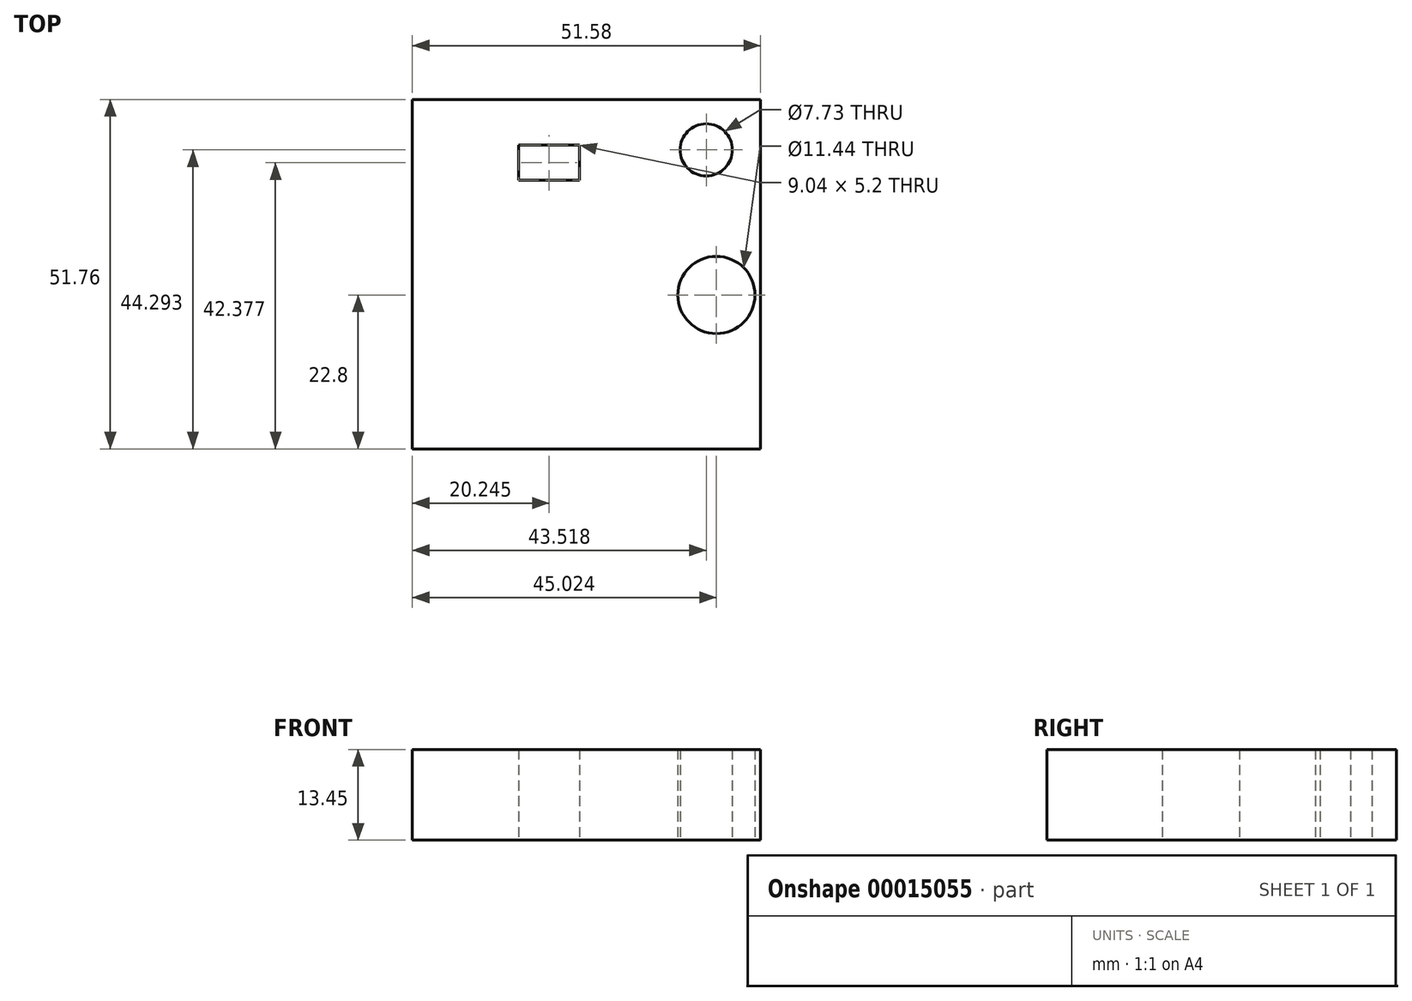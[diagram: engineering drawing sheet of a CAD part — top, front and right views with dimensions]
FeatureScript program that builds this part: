
annotation { "Feature Type Name" : "Feature", "Feature Type Description" : "" }
export const myFeature = defineFeature(function(context is Context, id is Id, definition is map)
    precondition{}
    {
        {
            var Q0;
            Q0=qCreatedBy(makeId("Top.planeOp"),FACE);
            var sketch = newSketch(context, id + "F0", { "sketchPlane" : qUnion([Q0])});
            skLineSegment(sketch, "E0.bottom", {"start": v(0, 0) * mm, "end": v(-51.58, 0) * mm});
            skLineSegment(sketch, "E0.top", {"start": v(0, 51.76) * mm, "end": v(-51.58, 51.76) * mm});
            skLineSegment(sketch, "E0.left", {"start": v(0, 0) * mm, "end": v(0, 51.76) * mm});
            skLineSegment(sketch, "E0.right", {"start": v(-51.58, 0) * mm, "end": v(-51.58, 51.76) * mm});
            skSolve(sketch);
        }
        {
            var Q0;
            Q0 = qSketchRegion(id + "F0", true);
            extrude(context, id + "F1", {"entities" : qUnion([Q0]), "depth" : 13.45 * mm});
        }
        {
            var Q0;
            Q0=makeQuery(id+"F1.opExtrude","CAP_FACE",FACE,{"disambiguationData":[OSD([sQuery(id+"F0.wireOp",EDGE,"E0.bottom"),sQuery(id+"F0.wireOp",EDGE,"E0.top"),sQuery(id+"F0.wireOp",EDGE,"E0.left"),sQuery(id+"F0.wireOp",EDGE,"E0.right")])],"isStart":true});
            var sketch = newSketch(context, id + "F2", { "sketchPlane" : qUnion([Q0])});
            skCircle(sketch, "E1", {"center": v(-8.06, -44.3) * mm, "radius": 3.86 * mm});
            skCircle(sketch, "E2", {"center": v(-35.58, -22.39) * mm, "radius": 6 * mm});
            skSolve(sketch);
        }
        {
            var Q0;
            Q0=makeQuery(id+"F2.imprint","IMPRINT",FACE,{"disambiguationData":[TD([[makeQuery(id+"F2.imprint","IMPRINT",EDGE,{"derivedFrom":sQuery(id+"F2.wireOp",EDGE,"E1")}),-1.0]])]});
            var sketch = newSketch(context, id + "F3", { "sketchPlane" : qUnion([Q0])});
            skCircle(sketch, "E3", {"center": v(-6.56, -22.8) * mm, "radius": 5.72 * mm});
            skLineSegment(sketch, "E4.bottom", {"start": v(-26.82, -44.98) * mm, "end": v(-35.85, -44.98) * mm});
            skLineSegment(sketch, "E4.top", {"start": v(-26.82, -39.78) * mm, "end": v(-35.85, -39.78) * mm});
            skLineSegment(sketch, "E4.left", {"start": v(-26.82, -44.98) * mm, "end": v(-26.82, -39.78) * mm});
            skLineSegment(sketch, "E4.right", {"start": v(-35.85, -44.98) * mm, "end": v(-35.85, -39.78) * mm});
            skSolve(sketch);
        }
        {
            var Q0;
            Q0=makeQuery(id+"F2.imprint","IMPRINT",FACE,{"disambiguationData":[TD([[makeQuery(id+"F2.imprint","IMPRINT",EDGE,{"derivedFrom":sQuery(id+"F2.wireOp",EDGE,"E1")}),1.0]])]});
            extrude(context, id + "F4", {"entities" : qUnion([Q0]), "operationType" : NewBodyOperationType.REMOVE, "oppositeDirection" : true, "depth" : 25 * mm});
        }
        {
            var Q0;
            Q0=makeQuery(id+"F3.imprint","IMPRINT",FACE,{"disambiguationData":[TD([[makeQuery(id+"F3.imprint","IMPRINT",EDGE,{"derivedFrom":sQuery(id+"F3.wireOp",EDGE,"E3")}),1.0]])]});
            var Q1;
            Q1=makeQuery(id+"F3.imprint","IMPRINT",FACE,{"disambiguationData":[TD([[makeQuery(id+"F3.imprint","IMPRINT",EDGE,{"derivedFrom":sQuery(id+"F3.wireOp",EDGE,"E4.bottom")}),-1.0]])]});
            extrude(context, id + "F5", {"entities" : qUnion([Q0, Q1]), "operationType" : NewBodyOperationType.REMOVE, "oppositeDirection" : true, "depth" : 25 * mm});
        }
    });
